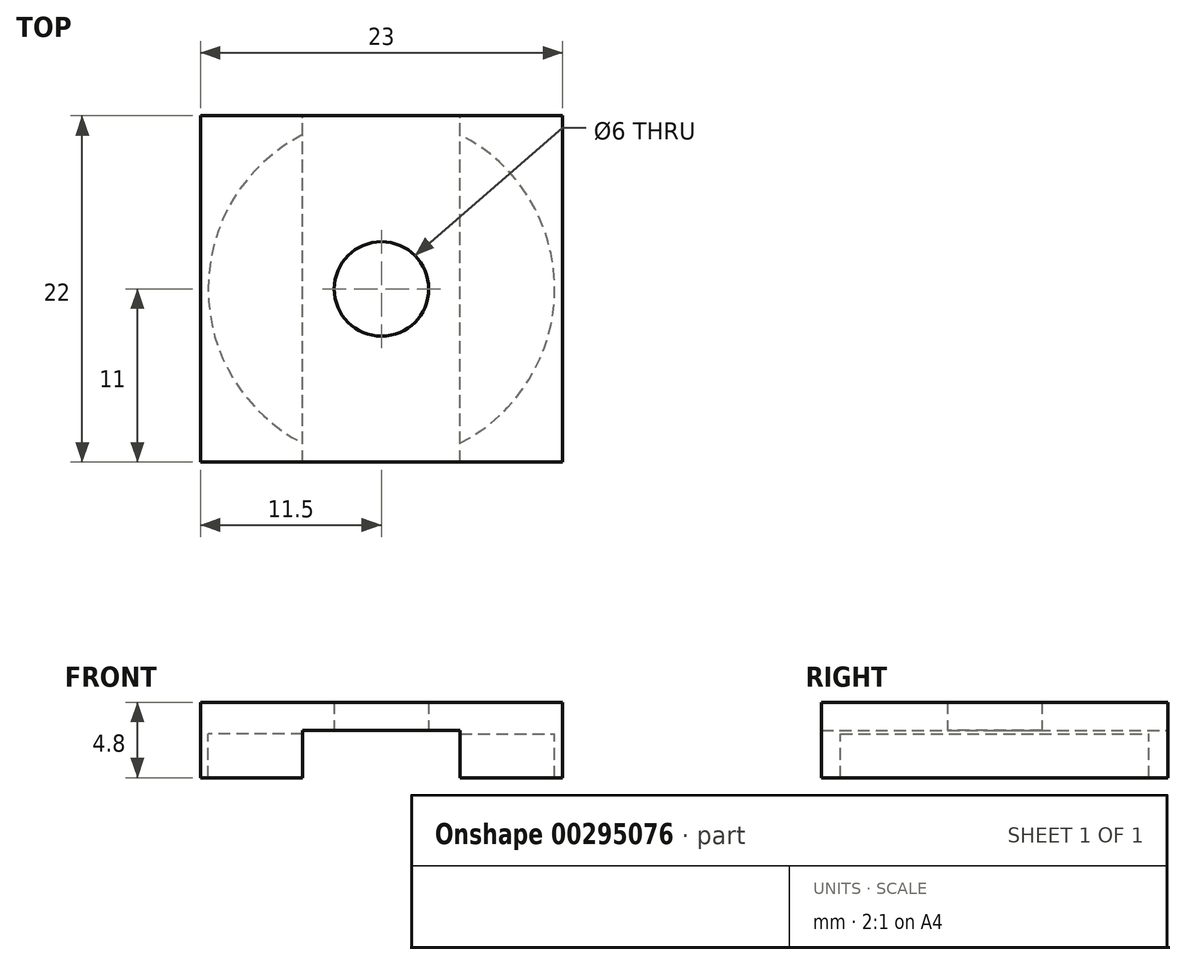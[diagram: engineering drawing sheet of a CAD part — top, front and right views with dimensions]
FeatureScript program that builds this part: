
annotation { "Feature Type Name" : "Feature", "Feature Type Description" : "" }
export const myFeature = defineFeature(function(context is Context, id is Id, definition is map)
    precondition{}
    {
        {
            var Q0;
            Q0=qCreatedBy(makeId("Top.planeOp"),FACE);
            var sketch = newSketch(context, id + "F0", { "sketchPlane" : qUnion([Q0])});
            skLineSegment(sketch, "E0.bottom", {"start": v(11.5, -11) * mm, "end": v(-11.5, -11) * mm});
            skLineSegment(sketch, "E0.top", {"start": v(11.5, 11) * mm, "end": v(-11.5, 11) * mm});
            skLineSegment(sketch, "E0.left", {"start": v(11.5, -11) * mm, "end": v(11.5, 11) * mm});
            skLineSegment(sketch, "E0.right", {"start": v(-11.5, -11) * mm, "end": v(-11.5, 11) * mm});
            skPoint(sketch, "E0.middle", {"position": v(0, 0) * mm});
            skCircle(sketch, "E1", {"center": v(0, 0) * mm, "radius": 3 * mm});
            skSolve(sketch);
        }
        {
            var Q0;
            Q0 = qSketchRegion(id + "F0", true);
            extrude(context, id + "F1", {"entities" : qUnion([Q0]), "depth" : 1.8 * mm});
        }
        {
            var Q0;
            Q0=makeQuery(id+"F1.opExtrude","CAP_FACE",FACE,{"disambiguationData":[OSD([sQuery(id+"F0.wireOp",EDGE,"E0.bottom"),sQuery(id+"F0.wireOp",EDGE,"E0.top"),sQuery(id+"F0.wireOp",EDGE,"E0.left"),sQuery(id+"F0.wireOp",EDGE,"E0.right")])],"isStart":true});
            var sketch = newSketch(context, id + "F2", { "sketchPlane" : qUnion([Q0])});
            skLineSegment(sketch, "E2", {"start": v(-5, 11) * mm, "end": v(-5, -11) * mm});
            skLineSegment(sketch, "E3", {"start": v(5, 11) * mm, "end": v(5, -11) * mm});
            skArc(sketch, "E4", {"start": v(-5, 9.8) * mm, "mid": v(-11, 0) * mm, "end": v(-5, -9.8) * mm});
            skArc(sketch, "E5.trimOffspring", {"start": v(5, -9.8) * mm, "mid": v(11, 0) * mm, "end": v(5, 9.8) * mm});
            skSolve(sketch);
        }
        {
            var Q0;
            {var subQ0=sQuery(id+"F2.wireOp",EDGE,"E4");Q0=makeQuery(id+"F2.imprint","IMPRINT",FACE,{"disambiguationData":[TD([[makeQuery(id+"F2.imprint","IMPRINT",EDGE,{"derivedFrom":subQ0}),1.0]])]});}
            var Q1;
            {var subQ0=sQuery(id+"F2.wireOp",EDGE,"E5.trimOffspring");Q1=makeQuery(id+"F2.imprint","IMPRINT",FACE,{"disambiguationData":[TD([[makeQuery(id+"F2.imprint","IMPRINT",EDGE,{"derivedFrom":subQ0}),1.0]])]});}
            extrude(context, id + "F3", {"entities" : qUnion([Q0, Q1]), "operationType" : NewBodyOperationType.ADD, "depth" : 0.2 * mm});
        }
        {
            var Q0;
            {var subQ1=sQuery(id+"F2.wireOp",EDGE,"E4");Q0=makeQuery(id+"F2.imprint","IMPRINT",FACE,{"disambiguationData":[TD([[makeQuery(id+"F2.imprint","IMPRINT",EDGE,{"derivedFrom":subQ1}),-1.0]])]});}
            var Q1;
            {var subQ0=sQuery(id+"F2.wireOp",EDGE,"E5.trimOffspring");Q1=makeQuery(id+"F2.imprint","IMPRINT",FACE,{"disambiguationData":[TD([[makeQuery(id+"F2.imprint","IMPRINT",EDGE,{"derivedFrom":subQ0}),-1.0]])]});}
            extrude(context, id + "F4", {"entities" : qUnion([Q0, Q1]), "operationType" : NewBodyOperationType.ADD, "depth" : 3 * mm});
        }
    });
